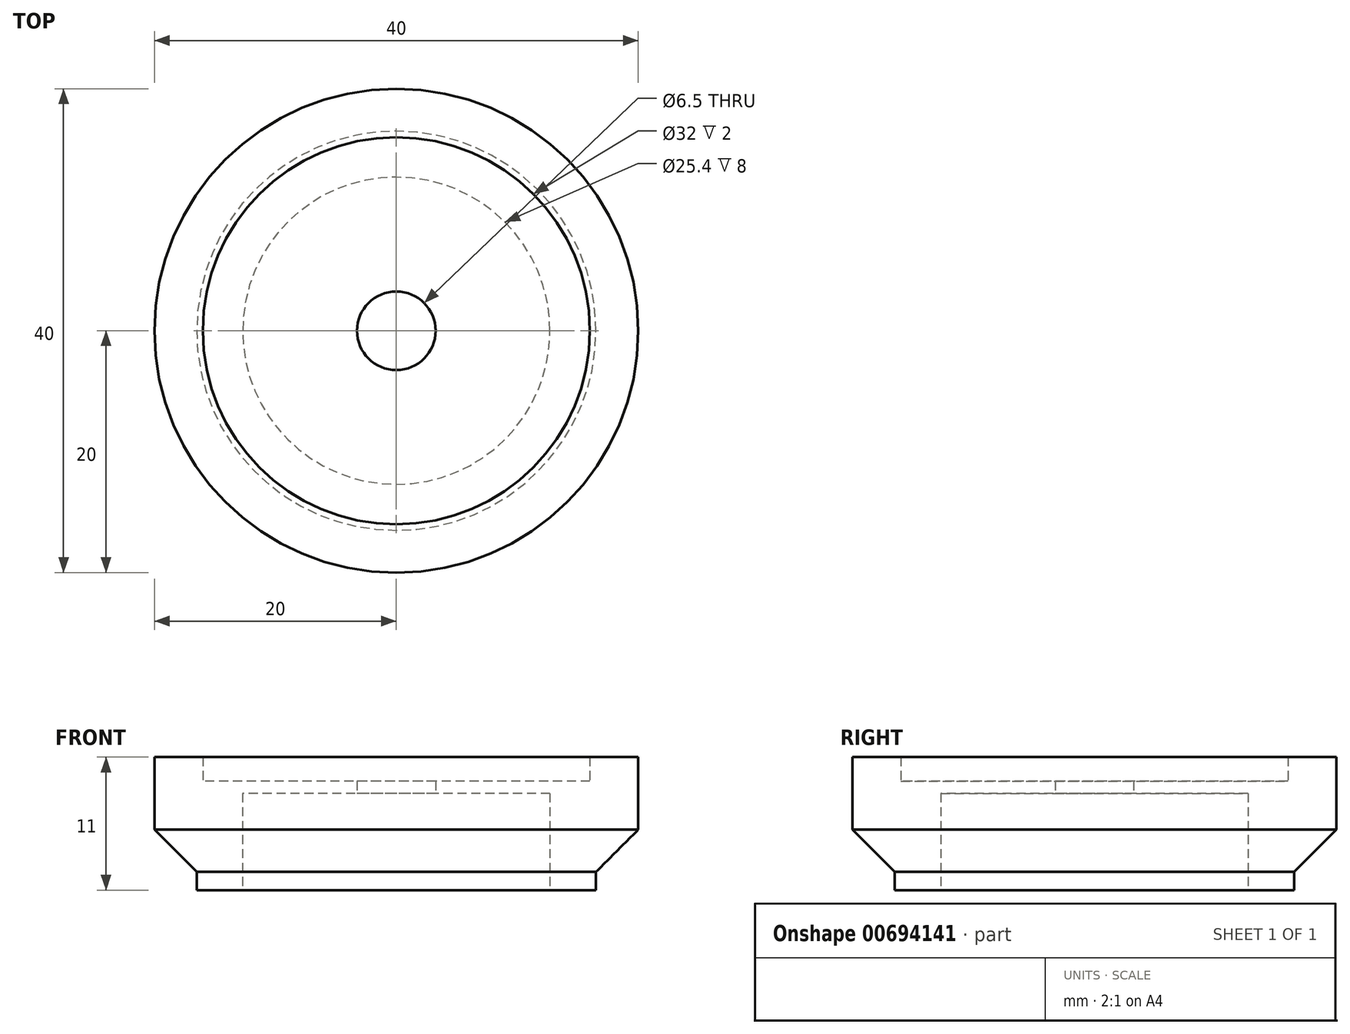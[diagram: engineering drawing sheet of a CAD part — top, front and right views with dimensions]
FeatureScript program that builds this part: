
annotation { "Feature Type Name" : "Feature", "Feature Type Description" : "" }
export const myFeature = defineFeature(function(context is Context, id is Id, definition is map)
    precondition{}
    {
        {
            var Q0;
            Q0=qCreatedBy(makeId("Top.planeOp"),FACE);
            var sketch = newSketch(context, id + "F0", { "sketchPlane" : qUnion([Q0])});
            skCircle(sketch, "E0", {"center": v(0, 0) * mm, "radius": 12.75 * mm});
            skCircle(sketch, "E1", {"center": v(0, 0) * mm, "radius": 20 * mm});
            skCircle(sketch, "E2", {"center": v(0, 0) * mm, "radius": 3.25 * mm});
            skSolve(sketch);
        }
        {
            var Q0;
            Q0=makeQuery(id+"F0.imprint","IMPRINT",FACE,{"disambiguationData":[TD([[makeQuery(id+"F0.imprint","IMPRINT",EDGE,{"derivedFrom":sQuery(id+"F0.wireOp",EDGE,"E0")}),1.0]])]});
            extrude(context, id + "F1", {"entities" : qUnion([Q0]), "depth" : 5 * mm, "offsetDistance" : 25 * mm});
        }
        {
            var Q0;
            Q0=makeQuery(id+"F0.imprint","IMPRINT",FACE,{"disambiguationData":[TD([[makeQuery(id+"F0.imprint","IMPRINT",EDGE,{"derivedFrom":sQuery(id+"F0.wireOp",EDGE,"E0")}),-1.0]])]});
            extrude(context, id + "F2", {"entities" : qUnion([Q0]), "operationType" : NewBodyOperationType.ADD, "depth" : 6 * mm, "offsetDistance" : 25 * mm, "hasSecondDirection" : true, "secondDirectionOppositeDirection" : true, "secondDirectionDepth" : 5 * mm});
        }
        {
            var Q0;
            Q0=makeQuery(id+"F2.opExtrude","CAP_EDGE",EDGE,{"disambiguationData":[OSD([sQuery(id+"F0.wireOp",EDGE,"E1")])],"isStart":true});
            chamfer(context, id + "F3", {"entities" : qUnion([Q0]), "width" : 5 * mm, "tangentPropagation" : true});
        }
        {
            var Q0;
            Q0=qCreatedBy(makeId("Top.planeOp"),FACE);
            var sketch = newSketch(context, id + "F4", { "sketchPlane" : qUnion([Q0])});
            skCircle(sketch, "E3", {"center": v(0, 0) * mm, "radius": 16 * mm});
            skSolve(sketch);
        }
        {
            var Q0;
            Q0 = qSketchRegion(id + "F4", true);
            extrude(context, id + "F5", {"entities" : qUnion([Q0]), "operationType" : NewBodyOperationType.REMOVE, "depth" : 3 * mm, "offsetDistance" : 25 * mm});
        }
        {
            var Q0;
            Q0 = qSketchRegion(id + "F4", true);
            extrude(context, id + "F6", {"entities" : qUnion([Q0]), "operationType" : NewBodyOperationType.REMOVE, "depth" : 25 * mm, "offsetDistance" : 25 * mm, "hasSecondDirection" : true, "secondDirectionOppositeDirection" : false, "secondDirectionDepth" : 4 * mm});
        }
        {
            var Q0;
            Q0=qCreatedBy(makeId("Top.planeOp"),FACE);
            var sketch = newSketch(context, id + "F7", { "sketchPlane" : qUnion([Q0])});
            skCircle(sketch, "E4", {"center": v(0, 0) * mm, "radius": 12.7 * mm});
            skCircle(sketch, "E5", {"center": v(0, 0) * mm, "radius": 16.5 * mm});
            skSolve(sketch);
        }
        {
            var Q0;
            Q0 = qSketchRegion(id + "F7", true);
            extrude(context, id + "F8", {"entities" : qUnion([Q0]), "operationType" : NewBodyOperationType.ADD, "depth" : 4 * mm, "offsetDistance" : 25 * mm, "hasSecondDirection" : true, "secondDirectionOppositeDirection" : true, "secondDirectionDepth" : 5 * mm});
        }
    });
